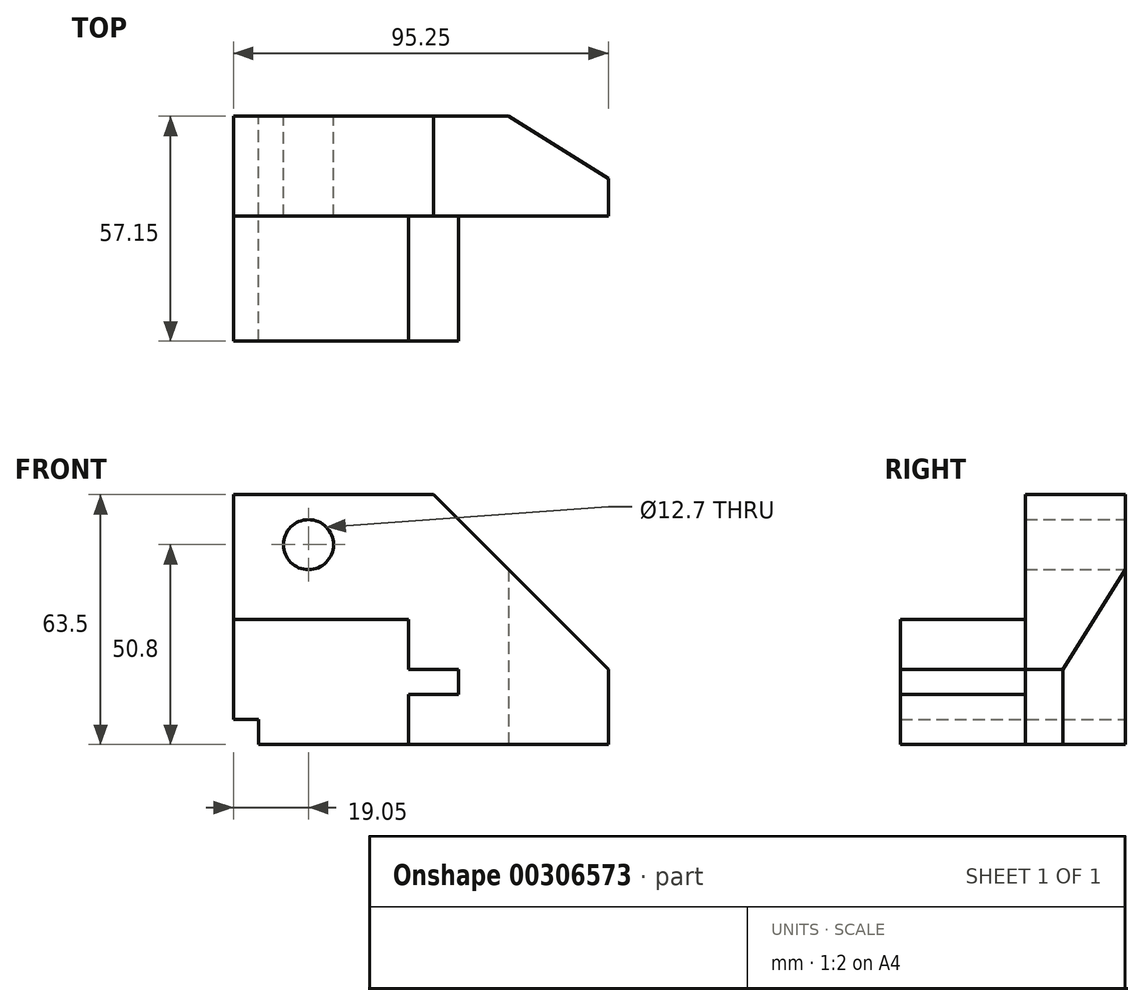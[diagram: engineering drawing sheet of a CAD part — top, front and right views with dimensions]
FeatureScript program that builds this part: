
annotation { "Feature Type Name" : "Feature", "Feature Type Description" : "" }
export const myFeature = defineFeature(function(context is Context, id is Id, definition is map)
    precondition{}
    {
        {
            var Q0;
            Q0=qCreatedBy(makeId("Front.planeOp"),FACE);
            var sketch = newSketch(context, id + "F0", { "sketchPlane" : qUnion([Q0])});
            skLineSegment(sketch, "E0", {"start": v(0, 0) * mm, "end": v(0, 6.35) * mm});
            skLineSegment(sketch, "E1", {"start": v(0, 6.35) * mm, "end": v(-6.35, 6.35) * mm});
            skLineSegment(sketch, "E2", {"start": v(-6.35, 6.35) * mm, "end": v(-6.35, 31.75) * mm});
            skLineSegment(sketch, "E3", {"start": v(-6.35, 31.75) * mm, "end": v(38.1, 31.75) * mm});
            skLineSegment(sketch, "E4", {"start": v(38.1, 31.75) * mm, "end": v(38.1, 19.05) * mm});
            skLineSegment(sketch, "E5", {"start": v(38.1, 19.05) * mm, "end": v(50.8, 19.05) * mm});
            skLineSegment(sketch, "E6", {"start": v(50.8, 19.05) * mm, "end": v(50.8, 12.7) * mm});
            skLineSegment(sketch, "E7", {"start": v(50.8, 12.7) * mm, "end": v(38.1, 12.7) * mm});
            skLineSegment(sketch, "E8", {"start": v(38.1, 12.7) * mm, "end": v(38.1, 0) * mm});
            skLineSegment(sketch, "E9", {"start": v(38.1, 0) * mm, "end": v(0, 0) * mm});
            skLineSegment(sketch, "E10", {"start": v(-6.35, 31.75) * mm, "end": v(-6.35, 63.5) * mm});
            skLineSegment(sketch, "E11", {"start": v(-6.35, 63.5) * mm, "end": v(44.45, 63.5) * mm});
            skLineSegment(sketch, "E12", {"start": v(44.45, 63.5) * mm, "end": v(88.9, 19.05) * mm});
            skLineSegment(sketch, "E13", {"start": v(88.9, 19.05) * mm, "end": v(88.9, 0) * mm});
            skLineSegment(sketch, "E14", {"start": v(88.9, 0) * mm, "end": v(38.1, 0) * mm});
            skCircle(sketch, "E15", {"center": v(12.7, 50.8) * mm, "radius": 6.35 * mm});
            skSolve(sketch);
        }
        {
            var Q0;
            Q0=makeQuery(id+"F0.imprint","IMPRINT",FACE,{"disambiguationData":[TD([[makeQuery(id+"F0.imprint","IMPRINT",EDGE,{"derivedFrom":sQuery(id+"F0.wireOp",EDGE,"E3")}),1.0]])]});
            extrude(context, id + "F1", {"entities" : qUnion([Q0]), "depth" : 25.4 * mm});
        }
        {
            var Q0;
            Q0=makeQuery(id+"F0.imprint","IMPRINT",FACE,{"disambiguationData":[TD([[makeQuery(id+"F0.imprint","IMPRINT",EDGE,{"derivedFrom":sQuery(id+"F0.wireOp",EDGE,"E0")}),-1.0]])]});
            extrude(context, id + "F2", {"entities" : qUnion([Q0]), "operationType" : NewBodyOperationType.ADD, "depth" : 57.15 * mm});
        }
        {
            var Q0;
            Q0=makeQuery(id+"F2.boolean.opBoolean","MERGE",FACE,{"derivedFrom":[makeQuery(id+"F1.opExtrude","SWEPT_FACE",FACE,{"disambiguationData":[OSD([sQuery(id+"F0.wireOp",EDGE,"E14")])]}),makeQuery(id+"F2.opExtrude","SWEPT_FACE",FACE,{"disambiguationData":[OSD([sQuery(id+"F0.wireOp",EDGE,"E9")])]})]});
            var sketch = newSketch(context, id + "F3", { "sketchPlane" : qUnion([Q0])});
            skLineSegment(sketch, "E16", {"start": v(88.9, 15.88) * mm, "end": v(63.5, 0) * mm});
            skLineSegment(sketch, "E17", {"start": v(88.9, 0) * mm, "end": v(63.5, 0) * mm});
            skSolve(sketch);
        }
        {
            var Q0;
            {var subQ0=sQuery(id+"F3.wireOp",EDGE,"E16");Q0=makeQuery(id+"F3.imprint","IMPRINT",FACE,{"disambiguationData":[TD([[makeQuery(id+"F3.imprint","IMPRINT",EDGE,{"derivedFrom":subQ0}),1.0]])]});}
            extrude(context, id + "F4", {"entities" : qUnion([Q0]), "operationType" : NewBodyOperationType.REMOVE, "oppositeDirection" : true, "depth" : 50.8 * mm});
        }
    });
